# Revit family: Шкаф антивандальный настенный ШАН-Н 19”
name_source: partatom
category: Обобщенные модели
units: mm (PartAtom-declared; Revit-internal decimal feet)

## family parameters
Всегда вертикально = Да
Может служить основой для арматурных стержней = Нет
На основе рабочей плоскости = Нет
Общий = Нет
При загрузке вырезать с полостями = Нет
Размер круглого соединителя = Использовать диаметр
Тип детали = Нормальный
Точка расчета площади = Нет

## types (3) — shared parameters
ADSK_URL документации изделия = https://www.ssd.ru
ADSK_URL страницы изделия = https://www.ssd.ru
ADSK_Единица измерения = шт.
ADSK_Завод-изготовитель = АО СВЯЗЬСТРОЙДЕТАЛЬ
ADSK_Количество = 1
ADSK_Материал обозначение = Серый RAL 7035
ADSK_Размер_Глубина = 550 мм
ADSK_Размер_Ширина = 600 мм

## per-type parameters (varying)
| type | ADSK_Код изделия | ADSK_Масса_Текст | ADSK_Обозначение | ADSK_Размер_Высота | Высота заклепок |
| Шкаф антивандальный напольный ШАН-Н 19", 18U ССД | 130411-011076 | 54,5 | ШАН-Н 18U | 914 мм | 915 мм |
| Шкаф антивандальный напольный ШАН-Н 19", 22U ССД | 130411-011077 | 61,7 | ШАН-Н 22U | 1092 мм | 1093 мм |
| Шкаф антивандальный напольный ШАН-Н 19", 30U ССД | 130411-011078 | 76,0 | ШАН-Н 30U | 1448 мм | 1449 мм |

note: column(s) folded — value = type name in every type: ADSK_Наименование
